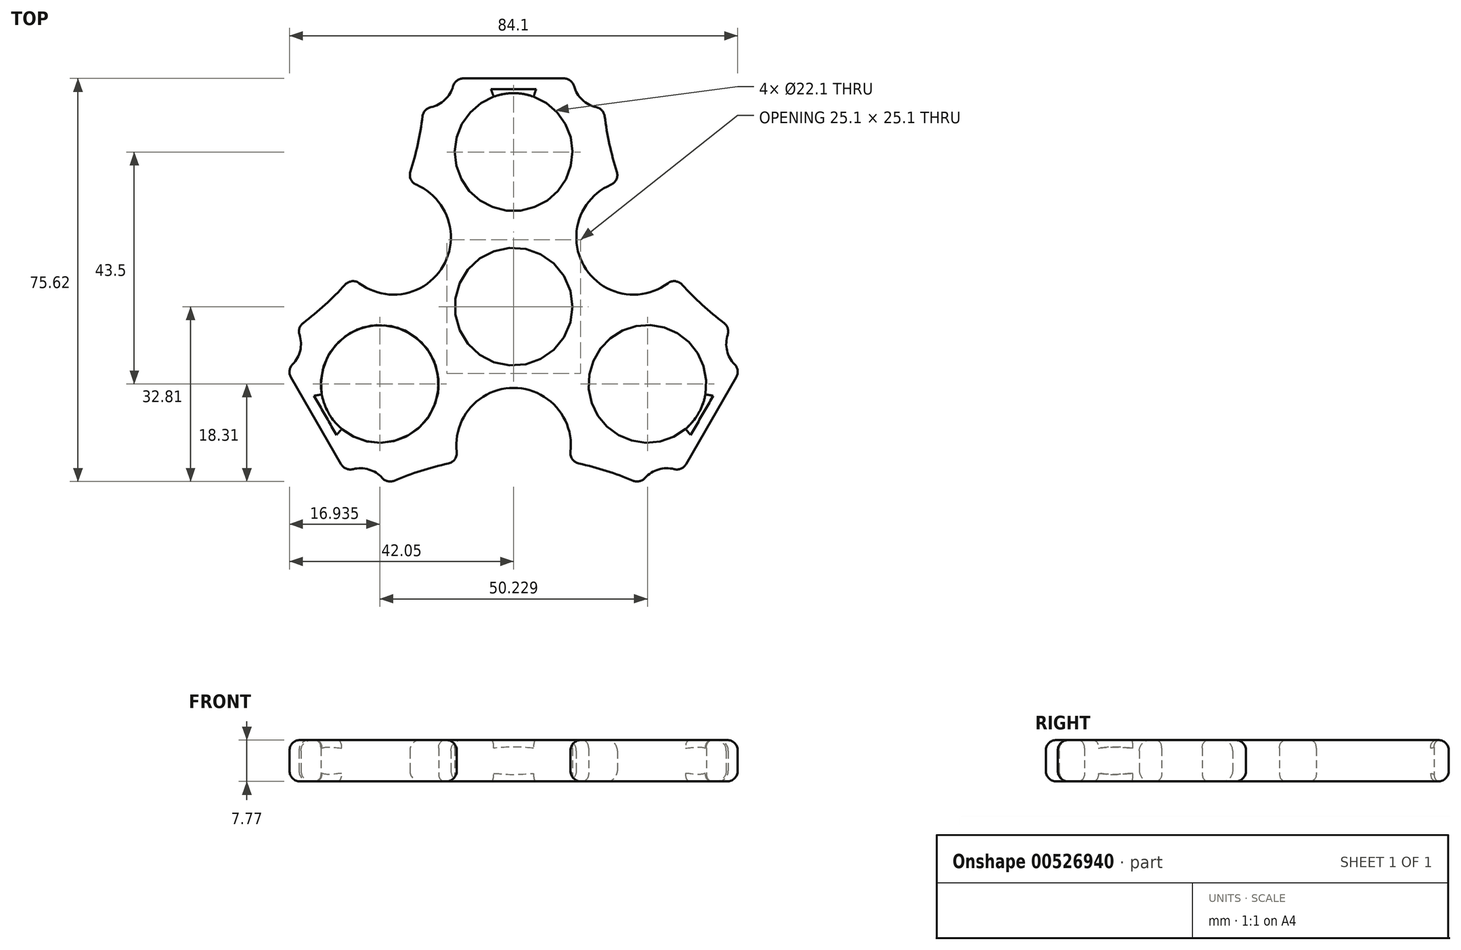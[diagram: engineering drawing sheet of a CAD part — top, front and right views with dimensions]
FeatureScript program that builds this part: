
annotation { "Feature Type Name" : "Feature", "Feature Type Description" : "" }
export const myFeature = defineFeature(function(context is Context, id is Id, definition is map)
    precondition{}
    {
        {
            var Q0;
            Q0=qCreatedBy(makeId("Top.planeOp"),FACE);
            var sketch = newSketch(context, id + "F0", { "sketchPlane" : qUnion([Q0])});
            skLineSegment(sketch, "E0", {"start": v(0, 0) * mm, "end": v(-25.11, -14.5) * mm});
            skLineSegment(sketch, "E1", {"start": v(-25.11, -14.5) * mm, "end": v(0, 0) * mm});
            skLineSegment(sketch, "E2", {"start": v(0, 0) * mm, "end": v(0, 29) * mm});
            skLineSegment(sketch, "E3", {"start": v(0, 29) * mm, "end": v(0, 0) * mm});
            skLineSegment(sketch, "E4", {"start": v(0, 0) * mm, "end": v(25.11, -14.5) * mm});
            skLineSegment(sketch, "E5", {"start": v(25.11, -14.5) * mm, "end": v(0, 0) * mm});
            skCircle(sketch, "E6", {"center": v(0, 29) * mm, "radius": 11.05 * mm});
            skCircle(sketch, "E7", {"center": v(-25.11, -14.5) * mm, "radius": 11.05 * mm});
            skCircle(sketch, "E8", {"center": v(25.11, -14.5) * mm, "radius": 11.05 * mm});
            skCircle(sketch, "E9", {"center": v(0, 0) * mm, "radius": 11.05 * mm});
            skCircle(sketch, "E10", {"center": v(-25.11, -14.5) * mm, "radius": 12.5 * mm});
            skCircle(sketch, "E11", {"center": v(0, 29) * mm, "radius": 12.5 * mm});
            skCircle(sketch, "E12", {"center": v(25.11, -14.5) * mm, "radius": 12.5 * mm});
            skLineSegment(sketch, "E13.0", {"start": v(74.15, 42.8) * mm, "end": v(0, -85.62) * mm});
            skLineSegment(sketch, "E13.1", {"start": v(0, -85.62) * mm, "end": v(-74.15, 42.8) * mm});
            skLineSegment(sketch, "E13.2", {"start": v(-74.15, 42.8) * mm, "end": v(74.15, 42.8) * mm});
            skPoint(sketch, "E13.0.midPoint", {"position": v(37.07, -21.4) * mm});
            skCircle(sketch, "E14", {"center": v(-74.15, 42.8) * mm, "radius": 57.5 * mm});
            skCircle(sketch, "E15", {"center": v(74.15, 42.8) * mm, "radius": 57.5 * mm});
            skCircle(sketch, "E16", {"center": v(0, -85.62) * mm, "radius": 57.5 * mm});
            skCircle(sketch, "E17", {"center": v(16.65, 42.8) * mm, "radius": 5.5 * mm});
            skCircle(sketch, "E18", {"center": v(-16.65, 42.8) * mm, "radius": 5.5 * mm});
            skCircle(sketch, "E19", {"center": v(-45.4, -6.99) * mm, "radius": 5.5 * mm});
            skCircle(sketch, "E20", {"center": v(-28.75, -35.82) * mm, "radius": 5.5 * mm});
            skCircle(sketch, "E21", {"center": v(28.75, -35.82) * mm, "radius": 5.5 * mm});
            skCircle(sketch, "E22", {"center": v(45.4, -6.99) * mm, "radius": 5.5 * mm});
            skLineSegment(sketch, "E23", {"start": v(25.11, -14.5) * mm, "end": v(-24.35, 14.06) * mm});
            skLineSegment(sketch, "E24", {"start": v(-25.11, -14.5) * mm, "end": v(24.35, 14.06) * mm});
            skLineSegment(sketch, "E25", {"start": v(0, 29) * mm, "end": v(0, -28.12) * mm});
            skCircle(sketch, "E26", {"center": v(22.52, 13) * mm, "radius": 10.75 * mm});
            skCircle(sketch, "E27", {"center": v(0, -26) * mm, "radius": 10.75 * mm});
            skCircle(sketch, "E28", {"center": v(-22.52, 13) * mm, "radius": 10.75 * mm});
            skSolve(sketch);
        }
        {
            var Q0;
            Q0=makeQuery(id+"F0.imprint","IMPRINT",FACE,{"disambiguationData":[TD([[makeQuery(id+"F0.imprint","IMPRINT",EDGE,{"derivedFrom":sQuery(id+"F0.wireOp",EDGE,"E11")}),-1.0]])]});
            var Q1;
            Q1=makeQuery(id+"F0.imprint","IMPRINT",FACE,{"disambiguationData":[TD([[makeQuery(id+"F0.imprint","IMPRINT",EDGE,{"derivedFrom":sQuery(id+"F0.wireOp",EDGE,"E10")}),-1.0]])]});
            var Q2;
            Q2=makeQuery(id+"F0.imprint","IMPRINT",FACE,{"disambiguationData":[TD([[makeQuery(id+"F0.imprint","IMPRINT",EDGE,{"derivedFrom":sQuery(id+"F0.wireOp",EDGE,"E12")}),-1.0]])]});
            var Q3;
            Q3=makeQuery(id+"F0.imprint","IMPRINT",FACE,{"disambiguationData":[TD([[makeQuery(id+"F0.imprint","IMPRINT",EDGE,{"derivedFrom":sQuery(id+"F0.wireOp",EDGE,"E6")}),-1.0]])]});
            var Q4;
            Q4=makeQuery(id+"F0.imprint","IMPRINT",FACE,{"disambiguationData":[TD([[makeQuery(id+"F0.imprint","IMPRINT",EDGE,{"derivedFrom":sQuery(id+"F0.wireOp",EDGE,"E7")}),-1.0]])]});
            var Q5;
            Q5=makeQuery(id+"F0.imprint","IMPRINT",FACE,{"disambiguationData":[TD([[makeQuery(id+"F0.imprint","IMPRINT",EDGE,{"derivedFrom":sQuery(id+"F0.wireOp",EDGE,"E8")}),-1.0]])]});
            extrude(context, id + "F1", {"entities" : qUnion([Q0, Q1, Q2, Q3, Q4, Q5]), "depth" : 7.77 * mm, "offsetDistance" : 25 * mm});
        }
        {
            var Q0;
            Q0=makeQuery(id+"F1.opExtrude","CAP_EDGE",EDGE,{"disambiguationData":[OSD([sQuery(id+"F0.wireOp",EDGE,"E13.2")])],"isStart":false});
            var Q1;
            Q1=makeQuery(id+"F1.opExtrude","CAP_EDGE",EDGE,{"disambiguationData":[OSD([sQuery(id+"F0.wireOp",EDGE,"E18")])],"isStart":true});
            var Q2;
            {var subQ0=sQuery(id+"F0.wireOp",EDGE,"E14");Q2=makeQuery(id+"F1.opExtrude","CAP_EDGE",EDGE,{"disambiguationData":[OSD([subQ0]),TDD([makeQuery(id+"F0.imprint","IMPRINT",EDGE,{"disambiguationData":[TD([[makeQuery(id+"F0.imprint","INTERSECT",VERTEX,{"disambiguationData":[OD(1.0)],"derivedFrom":[subQ0,sQuery(id+"F0.wireOp",EDGE,"tso12NrA-vn6K-p382-kDVD-uUXhCmWPkcJA")]}),-1.0]])],"derivedFrom":subQ0})])],"isStart":false});}
            var Q3;
            Q3=makeQuery(id+"F1.opExtrude","CAP_EDGE",EDGE,{"disambiguationData":[OSD([sQuery(id+"F0.wireOp",EDGE,"E18")])],"isStart":false});
            var Q4;
            Q4=makeQuery(id+"F1.opExtrude","CAP_EDGE",EDGE,{"disambiguationData":[OSD([sQuery(id+"F0.wireOp",EDGE,"tso12NrA-vn6K-p382-kDVD-uUXhCmWPkcJA")])],"isStart":false});
            var Q5;
            {var subQ0=sQuery(id+"F0.wireOp",EDGE,"E14");Q5=makeQuery(id+"F1.opExtrude","CAP_EDGE",EDGE,{"disambiguationData":[OSD([subQ0]),TDD([makeQuery(id+"F0.imprint","IMPRINT",EDGE,{"disambiguationData":[TD([[makeQuery(id+"F0.imprint","INTERSECT",VERTEX,{"disambiguationData":[OD(1.0)],"derivedFrom":[subQ0,sQuery(id+"F0.wireOp",EDGE,"E19")]}),-1.0]])],"derivedFrom":subQ0})])],"isStart":false});}
            var Q6;
            Q6=makeQuery(id+"F1.opExtrude","CAP_EDGE",EDGE,{"disambiguationData":[OSD([sQuery(id+"F0.wireOp",EDGE,"E19")])],"isStart":false});
            var Q7;
            Q7=makeQuery(id+"F1.opExtrude","CAP_EDGE",EDGE,{"disambiguationData":[OSD([sQuery(id+"F0.wireOp",EDGE,"E13.1")])],"isStart":false});
            var Q8;
            Q8=makeQuery(id+"F1.opExtrude","CAP_EDGE",EDGE,{"disambiguationData":[OSD([sQuery(id+"F0.wireOp",EDGE,"E20")])],"isStart":false});
            var Q9;
            {var subQ0=sQuery(id+"F0.wireOp",EDGE,"E16");Q9=makeQuery(id+"F1.opExtrude","CAP_EDGE",EDGE,{"disambiguationData":[OSD([subQ0]),TDD([makeQuery(id+"F0.imprint","IMPRINT",EDGE,{"disambiguationData":[TD([[makeQuery(id+"F0.imprint","INTERSECT",VERTEX,{"disambiguationData":[OD(1.0)],"derivedFrom":[subQ0,sQuery(id+"F0.wireOp",EDGE,"W5DYfLWn-jYW6-ROIx-5Qjh-cELPhGJE8ypl")]}),-1.0]])],"derivedFrom":subQ0})])],"isStart":false});}
            var Q10;
            Q10=makeQuery(id+"F1.opExtrude","CAP_EDGE",EDGE,{"disambiguationData":[OSD([sQuery(id+"F0.wireOp",EDGE,"W5DYfLWn-jYW6-ROIx-5Qjh-cELPhGJE8ypl")])],"isStart":false});
            var Q11;
            {var subQ0=sQuery(id+"F0.wireOp",EDGE,"E16");Q11=makeQuery(id+"F1.opExtrude","CAP_EDGE",EDGE,{"disambiguationData":[OSD([subQ0]),TDD([makeQuery(id+"F0.imprint","IMPRINT",EDGE,{"disambiguationData":[TD([[makeQuery(id+"F0.imprint","INTERSECT",VERTEX,{"disambiguationData":[OD(1.0)],"derivedFrom":[subQ0,sQuery(id+"F0.wireOp",EDGE,"E21")]}),-1.0]])],"derivedFrom":subQ0})])],"isStart":false});}
            var Q12;
            Q12=makeQuery(id+"F1.opExtrude","CAP_EDGE",EDGE,{"disambiguationData":[OSD([sQuery(id+"F0.wireOp",EDGE,"E21")])],"isStart":false});
            var Q13;
            Q13=makeQuery(id+"F1.opExtrude","CAP_EDGE",EDGE,{"disambiguationData":[OSD([sQuery(id+"F0.wireOp",EDGE,"E13.0")])],"isStart":false});
            var Q14;
            Q14=makeQuery(id+"F1.opExtrude","CAP_EDGE",EDGE,{"disambiguationData":[OSD([sQuery(id+"F0.wireOp",EDGE,"E22")])],"isStart":false});
            var Q15;
            {var subQ0=sQuery(id+"F0.wireOp",EDGE,"E15");Q15=makeQuery(id+"F1.opExtrude","CAP_EDGE",EDGE,{"disambiguationData":[OSD([subQ0]),TDD([makeQuery(id+"F0.imprint","IMPRINT",EDGE,{"disambiguationData":[TD([[makeQuery(id+"F0.imprint","INTERSECT",VERTEX,{"disambiguationData":[OD(1.0)],"derivedFrom":[subQ0,sQuery(id+"F0.wireOp",EDGE,"gOxveVNV-1YZB-HPbS-OaDW-XKyIJjo2ujh9")]}),-1.0]])],"derivedFrom":subQ0})])],"isStart":false});}
            var Q16;
            Q16=makeQuery(id+"F1.opExtrude","CAP_EDGE",EDGE,{"disambiguationData":[OSD([sQuery(id+"F0.wireOp",EDGE,"gOxveVNV-1YZB-HPbS-OaDW-XKyIJjo2ujh9")])],"isStart":false});
            var Q17;
            {var subQ0=sQuery(id+"F0.wireOp",EDGE,"E15");Q17=makeQuery(id+"F1.opExtrude","CAP_EDGE",EDGE,{"disambiguationData":[OSD([subQ0]),TDD([makeQuery(id+"F0.imprint","IMPRINT",EDGE,{"disambiguationData":[TD([[makeQuery(id+"F0.imprint","INTERSECT",VERTEX,{"disambiguationData":[OD(1.0)],"derivedFrom":[subQ0,sQuery(id+"F0.wireOp",EDGE,"E17")]}),-1.0]])],"derivedFrom":subQ0})])],"isStart":false});}
            var Q18;
            Q18=makeQuery(id+"F1.opExtrude","CAP_EDGE",EDGE,{"disambiguationData":[OSD([sQuery(id+"F0.wireOp",EDGE,"E17")])],"isStart":false});
            var Q19;
            Q19=makeQuery(id+"F1.opExtrude","CAP_EDGE",EDGE,{"disambiguationData":[OSD([sQuery(id+"F0.wireOp",EDGE,"E13.2")])],"isStart":true});
            var Q20;
            Q20=makeQuery(id+"F1.opExtrude","CAP_EDGE",EDGE,{"disambiguationData":[OSD([sQuery(id+"F0.wireOp",EDGE,"E17")])],"isStart":true});
            var Q21;
            {var subQ0=sQuery(id+"F0.wireOp",EDGE,"E15");Q21=makeQuery(id+"F1.opExtrude","CAP_EDGE",EDGE,{"disambiguationData":[OSD([subQ0]),TDD([makeQuery(id+"F0.imprint","IMPRINT",EDGE,{"disambiguationData":[TD([[makeQuery(id+"F0.imprint","INTERSECT",VERTEX,{"disambiguationData":[OD(1.0)],"derivedFrom":[subQ0,sQuery(id+"F0.wireOp",EDGE,"E17")]}),-1.0]])],"derivedFrom":subQ0})])],"isStart":true});}
            var Q22;
            Q22=makeQuery(id+"F1.opExtrude","CAP_EDGE",EDGE,{"disambiguationData":[OSD([sQuery(id+"F0.wireOp",EDGE,"gOxveVNV-1YZB-HPbS-OaDW-XKyIJjo2ujh9")])],"isStart":true});
            var Q23;
            {var subQ0=sQuery(id+"F0.wireOp",EDGE,"E14");Q23=makeQuery(id+"F1.opExtrude","CAP_EDGE",EDGE,{"disambiguationData":[OSD([subQ0]),TDD([makeQuery(id+"F0.imprint","IMPRINT",EDGE,{"disambiguationData":[TD([[makeQuery(id+"F0.imprint","INTERSECT",VERTEX,{"disambiguationData":[OD(1.0)],"derivedFrom":[subQ0,sQuery(id+"F0.wireOp",EDGE,"tso12NrA-vn6K-p382-kDVD-uUXhCmWPkcJA")]}),-1.0]])],"derivedFrom":subQ0})])],"isStart":true});}
            var Q24;
            Q24=makeQuery(id+"F1.opExtrude","CAP_EDGE",EDGE,{"disambiguationData":[OSD([sQuery(id+"F0.wireOp",EDGE,"tso12NrA-vn6K-p382-kDVD-uUXhCmWPkcJA")])],"isStart":true});
            var Q25;
            {var subQ0=sQuery(id+"F0.wireOp",EDGE,"E15");Q25=makeQuery(id+"F1.opExtrude","CAP_EDGE",EDGE,{"disambiguationData":[OSD([subQ0]),TDD([makeQuery(id+"F0.imprint","IMPRINT",EDGE,{"disambiguationData":[TD([[makeQuery(id+"F0.imprint","INTERSECT",VERTEX,{"disambiguationData":[OD(1.0)],"derivedFrom":[subQ0,sQuery(id+"F0.wireOp",EDGE,"gOxveVNV-1YZB-HPbS-OaDW-XKyIJjo2ujh9")]}),-1.0]])],"derivedFrom":subQ0})])],"isStart":true});}
            var Q26;
            Q26=makeQuery(id+"F1.opExtrude","CAP_EDGE",EDGE,{"disambiguationData":[OSD([sQuery(id+"F0.wireOp",EDGE,"E22")])],"isStart":true});
            var Q27;
            Q27=makeQuery(id+"F1.opExtrude","CAP_EDGE",EDGE,{"disambiguationData":[OSD([sQuery(id+"F0.wireOp",EDGE,"E13.0")])],"isStart":true});
            var Q28;
            Q28=makeQuery(id+"F1.opExtrude","CAP_EDGE",EDGE,{"disambiguationData":[OSD([sQuery(id+"F0.wireOp",EDGE,"E21")])],"isStart":true});
            var Q29;
            {var subQ0=sQuery(id+"F0.wireOp",EDGE,"E16");Q29=makeQuery(id+"F1.opExtrude","CAP_EDGE",EDGE,{"disambiguationData":[OSD([subQ0]),TDD([makeQuery(id+"F0.imprint","IMPRINT",EDGE,{"disambiguationData":[TD([[makeQuery(id+"F0.imprint","INTERSECT",VERTEX,{"disambiguationData":[OD(1.0)],"derivedFrom":[subQ0,sQuery(id+"F0.wireOp",EDGE,"E21")]}),-1.0]])],"derivedFrom":subQ0})])],"isStart":true});}
            var Q30;
            Q30=makeQuery(id+"F1.opExtrude","CAP_EDGE",EDGE,{"disambiguationData":[OSD([sQuery(id+"F0.wireOp",EDGE,"W5DYfLWn-jYW6-ROIx-5Qjh-cELPhGJE8ypl")])],"isStart":true});
            var Q31;
            {var subQ0=sQuery(id+"F0.wireOp",EDGE,"E16");Q31=makeQuery(id+"F1.opExtrude","CAP_EDGE",EDGE,{"disambiguationData":[OSD([subQ0]),TDD([makeQuery(id+"F0.imprint","IMPRINT",EDGE,{"disambiguationData":[TD([[makeQuery(id+"F0.imprint","INTERSECT",VERTEX,{"disambiguationData":[OD(1.0)],"derivedFrom":[subQ0,sQuery(id+"F0.wireOp",EDGE,"W5DYfLWn-jYW6-ROIx-5Qjh-cELPhGJE8ypl")]}),-1.0]])],"derivedFrom":subQ0})])],"isStart":true});}
            var Q32;
            Q32=makeQuery(id+"F1.opExtrude","CAP_EDGE",EDGE,{"disambiguationData":[OSD([sQuery(id+"F0.wireOp",EDGE,"E20")])],"isStart":true});
            var Q33;
            Q33=makeQuery(id+"F1.opExtrude","CAP_EDGE",EDGE,{"disambiguationData":[OSD([sQuery(id+"F0.wireOp",EDGE,"E13.1")])],"isStart":true});
            var Q34;
            Q34=makeQuery(id+"F1.opExtrude","CAP_EDGE",EDGE,{"disambiguationData":[OSD([sQuery(id+"F0.wireOp",EDGE,"E19")])],"isStart":true});
            var Q35;
            {var subQ0=sQuery(id+"F0.wireOp",EDGE,"E14");Q35=makeQuery(id+"F1.opExtrude","CAP_EDGE",EDGE,{"disambiguationData":[OSD([subQ0]),TDD([makeQuery(id+"F0.imprint","IMPRINT",EDGE,{"disambiguationData":[TD([[makeQuery(id+"F0.imprint","INTERSECT",VERTEX,{"disambiguationData":[OD(1.0)],"derivedFrom":[subQ0,sQuery(id+"F0.wireOp",EDGE,"E19")]}),-1.0]])],"derivedFrom":subQ0})])],"isStart":true});}
            var Q36;
            {var subQ0=sQuery(id+"F0.wireOp",EDGE,"W5DYfLWn-jYW6-ROIx-5Qjh-cELPhGJE8ypl");var subQ1=sQuery(id+"F0.wireOp",EDGE,"E16");Q36=makeQuery(id+"F1.opExtrude","SWEPT_EDGE",EDGE,{"disambiguationData":[OSD([subQ1,subQ0]),TDD([makeQuery(id+"F0.imprint","INTERSECT",VERTEX,{"disambiguationData":[OD(1.0)],"derivedFrom":[subQ1,subQ0]})])]});}
            var Q37;
            Q37=makeQuery(id+"F1.opExtrude","SWEPT_EDGE",EDGE,{"disambiguationData":[OSD([sQuery(id+"F0.wireOp",EDGE,"E16"),sQuery(id+"F0.wireOp",EDGE,"E20")])]});
            var Q38;
            Q38=makeQuery(id+"F1.opExtrude","SWEPT_EDGE",EDGE,{"disambiguationData":[OSD([sQuery(id+"F0.wireOp",EDGE,"E13.1"),sQuery(id+"F0.wireOp",EDGE,"E20")])]});
            var Q39;
            Q39=makeQuery(id+"F1.opExtrude","SWEPT_EDGE",EDGE,{"disambiguationData":[OSD([sQuery(id+"F0.wireOp",EDGE,"E13.1"),sQuery(id+"F0.wireOp",EDGE,"E19")])]});
            var Q40;
            Q40=makeQuery(id+"F1.opExtrude","SWEPT_EDGE",EDGE,{"disambiguationData":[OSD([sQuery(id+"F0.wireOp",EDGE,"E14"),sQuery(id+"F0.wireOp",EDGE,"E19")])]});
            var Q41;
            {var subQ0=sQuery(id+"F0.wireOp",EDGE,"tso12NrA-vn6K-p382-kDVD-uUXhCmWPkcJA");var subQ1=sQuery(id+"F0.wireOp",EDGE,"E14");Q41=makeQuery(id+"F1.opExtrude","SWEPT_EDGE",EDGE,{"disambiguationData":[OSD([subQ1,subQ0]),TDD([makeQuery(id+"F0.imprint","INTERSECT",VERTEX,{"disambiguationData":[OD(0.0)],"derivedFrom":[subQ1,subQ0]})])]});}
            var Q42;
            {var subQ0=sQuery(id+"F0.wireOp",EDGE,"tso12NrA-vn6K-p382-kDVD-uUXhCmWPkcJA");var subQ1=sQuery(id+"F0.wireOp",EDGE,"E14");Q42=makeQuery(id+"F1.opExtrude","SWEPT_EDGE",EDGE,{"disambiguationData":[OSD([subQ1,subQ0]),TDD([makeQuery(id+"F0.imprint","INTERSECT",VERTEX,{"disambiguationData":[OD(1.0)],"derivedFrom":[subQ1,subQ0]})])]});}
            var Q43;
            Q43=makeQuery(id+"F1.opExtrude","SWEPT_EDGE",EDGE,{"disambiguationData":[OSD([sQuery(id+"F0.wireOp",EDGE,"E14"),sQuery(id+"F0.wireOp",EDGE,"E18")])]});
            var Q44;
            Q44=makeQuery(id+"F1.opExtrude","SWEPT_EDGE",EDGE,{"disambiguationData":[OSD([sQuery(id+"F0.wireOp",EDGE,"E13.2"),sQuery(id+"F0.wireOp",EDGE,"E18")])]});
            var Q45;
            Q45=makeQuery(id+"F1.opExtrude","SWEPT_EDGE",EDGE,{"disambiguationData":[OSD([sQuery(id+"F0.wireOp",EDGE,"E13.2"),sQuery(id+"F0.wireOp",EDGE,"E17")])]});
            var Q46;
            Q46=makeQuery(id+"F1.opExtrude","SWEPT_EDGE",EDGE,{"disambiguationData":[OSD([sQuery(id+"F0.wireOp",EDGE,"E15"),sQuery(id+"F0.wireOp",EDGE,"E17")])]});
            var Q47;
            {var subQ0=sQuery(id+"F0.wireOp",EDGE,"gOxveVNV-1YZB-HPbS-OaDW-XKyIJjo2ujh9");var subQ1=sQuery(id+"F0.wireOp",EDGE,"E15");Q47=makeQuery(id+"F1.opExtrude","SWEPT_EDGE",EDGE,{"disambiguationData":[OSD([subQ1,subQ0]),TDD([makeQuery(id+"F0.imprint","INTERSECT",VERTEX,{"disambiguationData":[OD(0.0)],"derivedFrom":[subQ1,subQ0]})])]});}
            var Q48;
            Q48=makeQuery(id+"F1.opExtrude","SWEPT_EDGE",EDGE,{"disambiguationData":[OSD([sQuery(id+"F0.wireOp",EDGE,"E15"),sQuery(id+"F0.wireOp",EDGE,"E22")])]});
            var Q49;
            Q49=makeQuery(id+"F1.opExtrude","SWEPT_EDGE",EDGE,{"disambiguationData":[OSD([sQuery(id+"F0.wireOp",EDGE,"E13.0"),sQuery(id+"F0.wireOp",EDGE,"E22")])]});
            var Q50;
            {var subQ0=sQuery(id+"F0.wireOp",EDGE,"gOxveVNV-1YZB-HPbS-OaDW-XKyIJjo2ujh9");var subQ1=sQuery(id+"F0.wireOp",EDGE,"E15");Q50=makeQuery(id+"F1.opExtrude","SWEPT_EDGE",EDGE,{"disambiguationData":[OSD([subQ1,subQ0]),TDD([makeQuery(id+"F0.imprint","INTERSECT",VERTEX,{"disambiguationData":[OD(1.0)],"derivedFrom":[subQ1,subQ0]})])]});}
            var Q51;
            Q51=makeQuery(id+"F1.opExtrude","SWEPT_EDGE",EDGE,{"disambiguationData":[OSD([sQuery(id+"F0.wireOp",EDGE,"E16"),sQuery(id+"F0.wireOp",EDGE,"E21")])]});
            var Q52;
            Q52=makeQuery(id+"F1.opExtrude","SWEPT_FACE",FACE,{"disambiguationData":[OSD([sQuery(id+"F0.wireOp",EDGE,"W5DYfLWn-jYW6-ROIx-5Qjh-cELPhGJE8ypl")])]});
            var Q53;
            {var subQ0=sQuery(id+"F0.wireOp",EDGE,"E28");var subQ1=sQuery(id+"F0.wireOp",EDGE,"E14");Q53=makeQuery(id+"F1.opExtrude","SWEPT_EDGE",EDGE,{"disambiguationData":[OSD([subQ1,subQ0]),TDD([makeQuery(id+"F0.imprint","INTERSECT",VERTEX,{"disambiguationData":[OD(1.0)],"derivedFrom":[subQ1,subQ0]})])]});}
            var Q54;
            {var subQ0=sQuery(id+"F0.wireOp",EDGE,"E27");var subQ1=sQuery(id+"F0.wireOp",EDGE,"E16");Q54=makeQuery(id+"F1.opExtrude","SWEPT_EDGE",EDGE,{"disambiguationData":[OSD([subQ1,subQ0]),TDD([makeQuery(id+"F0.imprint","INTERSECT",VERTEX,{"disambiguationData":[OD(1.0)],"derivedFrom":[subQ1,subQ0]})])]});}
            var Q55;
            {var subQ0=sQuery(id+"F0.wireOp",EDGE,"E28");var subQ1=sQuery(id+"F0.wireOp",EDGE,"E14");Q55=makeQuery(id+"F1.opExtrude","SWEPT_EDGE",EDGE,{"disambiguationData":[OSD([subQ1,subQ0]),TDD([makeQuery(id+"F0.imprint","INTERSECT",VERTEX,{"disambiguationData":[OD(0.0)],"derivedFrom":[subQ1,subQ0]})])]});}
            var Q56;
            {var subQ0=sQuery(id+"F0.wireOp",EDGE,"E26");var subQ1=sQuery(id+"F0.wireOp",EDGE,"E15");Q56=makeQuery(id+"F1.opExtrude","SWEPT_EDGE",EDGE,{"disambiguationData":[OSD([subQ1,subQ0]),TDD([makeQuery(id+"F0.imprint","INTERSECT",VERTEX,{"disambiguationData":[OD(1.0)],"derivedFrom":[subQ1,subQ0]})])]});}
            var Q57;
            {var subQ0=sQuery(id+"F0.wireOp",EDGE,"E26");var subQ1=sQuery(id+"F0.wireOp",EDGE,"E15");Q57=makeQuery(id+"F1.opExtrude","SWEPT_EDGE",EDGE,{"disambiguationData":[OSD([subQ1,subQ0]),TDD([makeQuery(id+"F0.imprint","INTERSECT",VERTEX,{"disambiguationData":[OD(0.0)],"derivedFrom":[subQ1,subQ0]})])]});}
            var Q58;
            {var subQ0=sQuery(id+"F0.wireOp",EDGE,"E27");var subQ1=sQuery(id+"F0.wireOp",EDGE,"E16");Q58=makeQuery(id+"F1.opExtrude","SWEPT_EDGE",EDGE,{"disambiguationData":[OSD([subQ1,subQ0]),TDD([makeQuery(id+"F0.imprint","INTERSECT",VERTEX,{"disambiguationData":[OD(0.0)],"derivedFrom":[subQ1,subQ0]})])]});}
            var Q59;
            Q59=makeQuery(id+"F1.opExtrude","CAP_EDGE",EDGE,{"disambiguationData":[OSD([sQuery(id+"F0.wireOp",EDGE,"E28")])],"isStart":true});
            var Q60;
            Q60=makeQuery(id+"F1.opExtrude","CAP_EDGE",EDGE,{"disambiguationData":[OSD([sQuery(id+"F0.wireOp",EDGE,"E26")])],"isStart":true});
            var Q61;
            Q61=makeQuery(id+"F1.opExtrude","CAP_EDGE",EDGE,{"disambiguationData":[OSD([sQuery(id+"F0.wireOp",EDGE,"E27")])],"isStart":true});
            var Q62;
            Q62=makeQuery(id+"F1.opExtrude","CAP_EDGE",EDGE,{"disambiguationData":[OSD([sQuery(id+"F0.wireOp",EDGE,"E28")])],"isStart":false});
            var Q63;
            Q63=makeQuery(id+"F1.opExtrude","CAP_EDGE",EDGE,{"disambiguationData":[OSD([sQuery(id+"F0.wireOp",EDGE,"E26")])],"isStart":false});
            var Q64;
            Q64=makeQuery(id+"F1.opExtrude","CAP_EDGE",EDGE,{"disambiguationData":[OSD([sQuery(id+"F0.wireOp",EDGE,"E27")])],"isStart":false});
            var Q65;
            {var subQ0=sQuery(id+"F0.wireOp",EDGE,"E15");Q65=makeQuery(id+"F1.opExtrude","SWEPT_FACE",FACE,{"disambiguationData":[OSD([subQ0]),TDD([makeQuery(id+"F0.imprint","IMPRINT",EDGE,{"disambiguationData":[TD([[makeQuery(id+"F0.imprint","INTERSECT",VERTEX,{"disambiguationData":[OD(1.0)],"derivedFrom":[subQ0,sQuery(id+"F0.wireOp",EDGE,"E26")]}),-1.0]])],"derivedFrom":subQ0})])]});}
            var Q66;
            {var subQ0=sQuery(id+"F0.wireOp",EDGE,"E14");Q66=makeQuery(id+"F1.opExtrude","CAP_EDGE",EDGE,{"disambiguationData":[OSD([subQ0]),TDD([makeQuery(id+"F0.imprint","IMPRINT",EDGE,{"disambiguationData":[TD([[makeQuery(id+"F0.imprint","INTERSECT",VERTEX,{"disambiguationData":[OD(1.0)],"derivedFrom":[subQ0,sQuery(id+"F0.wireOp",EDGE,"E28")]}),-1.0]])],"derivedFrom":subQ0})])],"isStart":false});}
            var Q67;
            {var subQ0=sQuery(id+"F0.wireOp",EDGE,"E16");Q67=makeQuery(id+"F1.opExtrude","SWEPT_FACE",FACE,{"disambiguationData":[OSD([subQ0]),TDD([makeQuery(id+"F0.imprint","IMPRINT",EDGE,{"disambiguationData":[TD([[makeQuery(id+"F0.imprint","INTERSECT",VERTEX,{"disambiguationData":[OD(1.0)],"derivedFrom":[subQ0,sQuery(id+"F0.wireOp",EDGE,"E27")]}),-1.0]])],"derivedFrom":subQ0})])]});}
            var Q68;
            {var subQ0=sQuery(id+"F0.wireOp",EDGE,"E14");Q68=makeQuery(id+"F1.opExtrude","CAP_EDGE",EDGE,{"disambiguationData":[OSD([subQ0]),TDD([makeQuery(id+"F0.imprint","IMPRINT",EDGE,{"disambiguationData":[TD([[makeQuery(id+"F0.imprint","INTERSECT",VERTEX,{"disambiguationData":[OD(1.0)],"derivedFrom":[subQ0,sQuery(id+"F0.wireOp",EDGE,"E28")]}),-1.0]])],"derivedFrom":subQ0})])],"isStart":true});}
            var Q69;
            Q69=makeQuery(id+"F1.opExtrude","SWEPT_EDGE",EDGE,{"disambiguationData":[OSD([sQuery(id+"F0.wireOp",EDGE,"E13.0"),sQuery(id+"F0.wireOp",EDGE,"E21")])]});
            fillet(context, id + "F2", {"entities" : qUnion([Q0, Q1, Q2, Q3, Q4, Q5, Q6, Q7, Q8, Q9, Q10, Q11, Q12, Q13, Q14, Q15, Q16, Q17, Q18, Q19, Q20, Q21, Q22, Q23, Q24, Q25, Q26, Q27, Q28, Q29, Q30, Q31, Q32, Q33, Q34, Q35, Q36, Q37, Q38, Q39, Q40, Q41, Q42, Q43, Q44, Q45, Q46, Q47, Q48, Q49, Q50, Q51, Q52, Q53, Q54, Q55, Q56, Q57, Q58, Q59, Q60, Q61, Q62, Q63, Q64, Q65, Q66, Q67, Q68, Q69]), "radius" : 2 * mm, "tangentPropagation" : true, "allowEdgeOverflow" : false});
        }
        {
            var Q0;
            Q0=makeQuery(id+"F1.opExtrude","CAP_EDGE",EDGE,{"disambiguationData":[OSD([sQuery(id+"F0.wireOp",EDGE,"E6")])],"isStart":true});
            var Q1;
            Q1=makeQuery(id+"F1.opExtrude","CAP_EDGE",EDGE,{"disambiguationData":[OSD([sQuery(id+"F0.wireOp",EDGE,"E6")])],"isStart":false});
            var Q2;
            Q2=makeQuery(id+"F1.opExtrude","CAP_EDGE",EDGE,{"disambiguationData":[OSD([sQuery(id+"F0.wireOp",EDGE,"E9")])],"isStart":false});
            var Q3;
            Q3=makeQuery(id+"F1.opExtrude","CAP_EDGE",EDGE,{"disambiguationData":[OSD([sQuery(id+"F0.wireOp",EDGE,"E7")])],"isStart":false});
            var Q4;
            Q4=makeQuery(id+"F1.opExtrude","CAP_EDGE",EDGE,{"disambiguationData":[OSD([sQuery(id+"F0.wireOp",EDGE,"E8")])],"isStart":false});
            var Q5;
            Q5=makeQuery(id+"F1.opExtrude","CAP_EDGE",EDGE,{"disambiguationData":[OSD([sQuery(id+"F0.wireOp",EDGE,"E8")])],"isStart":true});
            var Q6;
            Q6=makeQuery(id+"F1.opExtrude","CAP_EDGE",EDGE,{"disambiguationData":[OSD([sQuery(id+"F0.wireOp",EDGE,"E9")])],"isStart":true});
            var Q7;
            Q7=makeQuery(id+"F1.opExtrude","CAP_EDGE",EDGE,{"disambiguationData":[OSD([sQuery(id+"F0.wireOp",EDGE,"E7")])],"isStart":true});
            fillet(context, id + "F3", {"entities" : qUnion([Q0, Q1, Q2, Q3, Q4, Q5, Q6, Q7]), "radius" : 1.5 * mm, "rho" : 0.5, "crossSection" : FilletCrossSection.CONIC, "allowEdgeOverflow" : false});
        }
    });
